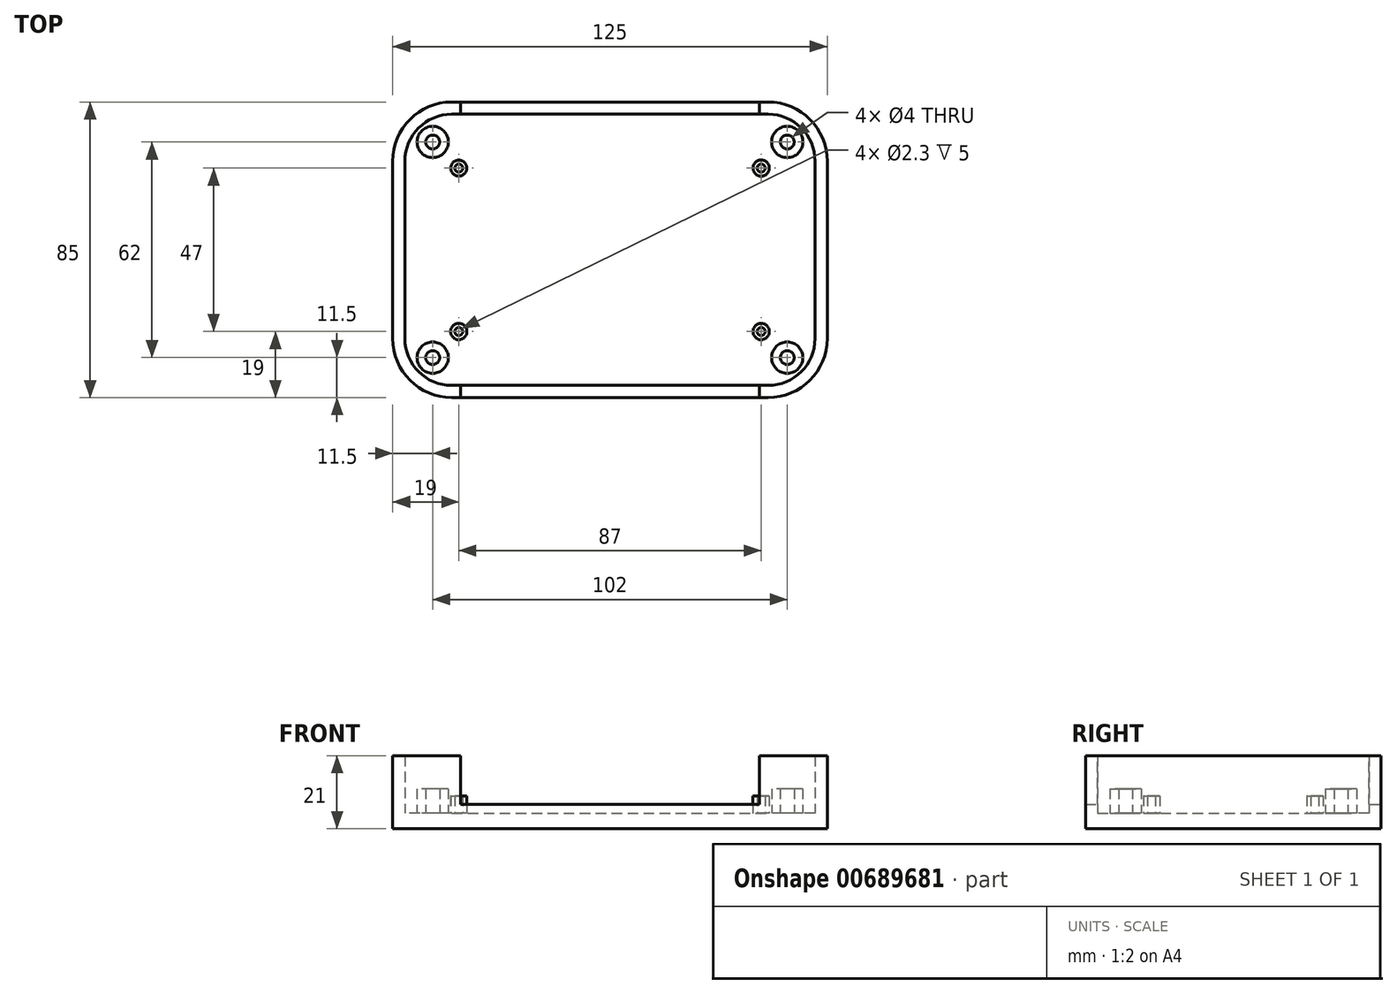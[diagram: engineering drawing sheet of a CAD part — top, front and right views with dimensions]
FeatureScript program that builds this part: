
annotation { "Feature Type Name" : "Feature", "Feature Type Description" : "" }
export const myFeature = defineFeature(function(context is Context, id is Id, definition is map)
    precondition{}
    {
        {
            var Q0;
            Q0=qCreatedBy(makeId("Top.planeOp"),FACE);
            var sketch = newSketch(context, id + "F0", { "sketchPlane" : qUnion([Q0])});
            skLineSegment(sketch, "E0.bottom", {"start": v(17, 0) * mm, "end": v(108, 0) * mm});
            skLineSegment(sketch, "E0.top", {"start": v(17, 85) * mm, "end": v(108, 85) * mm});
            skLineSegment(sketch, "E0.left", {"start": v(0, 17) * mm, "end": v(0, 68) * mm});
            skLineSegment(sketch, "E0.right", {"start": v(125, 17) * mm, "end": v(125, 68) * mm});
            skPoint(sketch, "E1.visualSharp", {"position": v(0, 85) * mm});
            skArc(sketch, "E1.filletArc", {"start": v(17, 85) * mm, "mid": v(4.98, 80.02) * mm, "end": v(0, 68) * mm});
            skPoint(sketch, "E2.visualSharp", {"position": v(125, 85) * mm});
            skArc(sketch, "E2.filletArc", {"start": v(125, 68) * mm, "mid": v(120.02, 80.02) * mm, "end": v(108, 85) * mm});
            skPoint(sketch, "E3.visualSharp", {"position": v(125, 0) * mm});
            skArc(sketch, "E3.filletArc", {"start": v(108, 0) * mm, "mid": v(120.02, 4.98) * mm, "end": v(125, 17) * mm});
            skPoint(sketch, "E4.visualSharp", {"position": v(0, 0) * mm});
            skArc(sketch, "E4.filletArc", {"start": v(0, 17) * mm, "mid": v(4.98, 4.98) * mm, "end": v(17, 0) * mm});
            skSolve(sketch);
        }
        {
            var Q0;
            Q0 = qSketchRegion(id + "F0", true);
            extrude(context, id + "F1", {"entities" : qUnion([Q0]), "oppositeDirection" : true, "depth" : 4.5 * mm, "offsetDistance" : 25.4 * mm});
        }
        {
            var Q0;
            Q0=qCreatedBy(makeId("Top.planeOp"),FACE);
            var sketch = newSketch(context, id + "F2", { "sketchPlane" : qUnion([Q0])});
            skCircle(sketch, "E5", {"center": v(11.5, 73.5) * mm, "radius": 4.5 * mm});
            skCircle(sketch, "E6", {"center": v(113.5, 73.5) * mm, "radius": 4.5 * mm});
            skCircle(sketch, "E7", {"center": v(11.5, 11.5) * mm, "radius": 4.5 * mm});
            skCircle(sketch, "E8", {"center": v(113.5, 11.5) * mm, "radius": 4.5 * mm});
            skCircle(sketch, "E9.0", {"center": v(11.5, 73.5) * mm, "radius": 2 * mm});
            skCircle(sketch, "E10", {"center": v(113.5, 73.5) * mm, "radius": 2 * mm});
            skCircle(sketch, "E11", {"center": v(11.5, 11.5) * mm, "radius": 2 * mm});
            skCircle(sketch, "E12", {"center": v(113.5, 11.5) * mm, "radius": 2 * mm});
            skSolve(sketch);
        }
        {
            var Q0;
            Q0 = qSketchRegion(id + "F2", true);
            extrude(context, id + "F3", {"entities" : qUnion([Q0]), "depth" : 7 * mm, "offsetDistance" : 25.4 * mm});
        }
        {
            var Q0;
            Q0=qCreatedBy(makeId("Top.planeOp"),FACE);
            var sketch = newSketch(context, id + "F4", { "sketchPlane" : qUnion([Q0])});
            skLineSegment(sketch, "E13.bottom", {"start": v(17, 0) * mm, "end": v(108, 0) * mm});
            skLineSegment(sketch, "E13.top", {"start": v(17, 85) * mm, "end": v(108, 85) * mm});
            skLineSegment(sketch, "E13.left", {"start": v(0, 17) * mm, "end": v(0, 68) * mm});
            skLineSegment(sketch, "E13.right", {"start": v(125, 17) * mm, "end": v(125, 68) * mm});
            skPoint(sketch, "E14.visualSharp", {"position": v(0, 85) * mm});
            skArc(sketch, "E14.filletArc", {"start": v(17, 85) * mm, "mid": v(4.98, 80.02) * mm, "end": v(0, 68) * mm});
            skPoint(sketch, "E15.visualSharp", {"position": v(0, 0) * mm});
            skArc(sketch, "E15.filletArc", {"start": v(0, 17) * mm, "mid": v(4.98, 4.98) * mm, "end": v(17, 0) * mm});
            skPoint(sketch, "E16.visualSharp", {"position": v(125, 0) * mm});
            skArc(sketch, "E16.filletArc", {"start": v(108, 0) * mm, "mid": v(120.02, 4.98) * mm, "end": v(125, 17) * mm});
            skPoint(sketch, "E17.visualSharp", {"position": v(125, 85) * mm});
            skArc(sketch, "E17.filletArc", {"start": v(125, 68) * mm, "mid": v(120.02, 80.02) * mm, "end": v(108, 85) * mm});
            skLineSegment(sketch, "E18.0", {"start": v(17, 81.5) * mm, "end": v(108, 81.5) * mm});
            skArc(sketch, "E18.1", {"start": v(121.5, 68) * mm, "mid": v(117.55, 77.55) * mm, "end": v(108, 81.5) * mm});
            skArc(sketch, "E18.2", {"start": v(17, 81.5) * mm, "mid": v(7.45, 77.55) * mm, "end": v(3.5, 68) * mm});
            skLineSegment(sketch, "E18.3", {"start": v(121.5, 17) * mm, "end": v(121.5, 68) * mm});
            skLineSegment(sketch, "E18.4", {"start": v(3.5, 17) * mm, "end": v(3.5, 68) * mm});
            skArc(sketch, "E18.5", {"start": v(3.5, 17) * mm, "mid": v(7.45, 7.45) * mm, "end": v(17, 3.5) * mm});
            skLineSegment(sketch, "E18.6", {"start": v(17, 3.5) * mm, "end": v(108, 3.5) * mm});
            skArc(sketch, "E18.7", {"start": v(108, 3.5) * mm, "mid": v(117.55, 7.45) * mm, "end": v(121.5, 17) * mm});
            skSolve(sketch);
        }
        {
            var Q0;
            Q0 = qSketchRegion(id + "F4", true);
            extrude(context, id + "F5", {"entities" : qUnion([Q0]), "operationType" : NewBodyOperationType.ADD, "depth" : 16.5 * mm, "offsetDistance" : 25.4 * mm});
        }
        {
            var Q0;
            Q0=qCreatedBy(makeId("Top.planeOp"),FACE);
            var sketch = newSketch(context, id + "F6", { "sketchPlane" : qUnion([Q0])});
            skCircle(sketch, "E19", {"center": v(19, 66) * mm, "radius": 2.3 * mm});
            skCircle(sketch, "E20", {"center": v(106, 66) * mm, "radius": 2.35 * mm});
            skCircle(sketch, "E21", {"center": v(106, 19) * mm, "radius": 2.35 * mm});
            skCircle(sketch, "E22", {"center": v(19, 19) * mm, "radius": 2.35 * mm});
            skCircle(sketch, "E23", {"center": v(19, 66) * mm, "radius": 1.15 * mm});
            skCircle(sketch, "E24", {"center": v(106, 66) * mm, "radius": 1.15 * mm});
            skCircle(sketch, "E25", {"center": v(106, 19) * mm, "radius": 1.15 * mm});
            skCircle(sketch, "E26", {"center": v(19, 19) * mm, "radius": 1.15 * mm});
            skSolve(sketch);
        }
        {
            var Q0;
            Q0 = qSketchRegion(id + "F6", true);
            extrude(context, id + "F7", {"entities" : qUnion([Q0]), "operationType" : NewBodyOperationType.ADD, "depth" : 5 * mm, "offsetDistance" : 25.4 * mm});
        }
        {
            var Q0;
            Q0=qCreatedBy(makeId("Top.planeOp"),FACE);
            cPlane(context, id + "F8", {"entities" : qUnion([Q0]), "cplaneType" : CPlaneType.OFFSET, "offset" : 2.5 * mm, "width" : 152.4 * mm, "height" : 152.4 * mm});
        }
        {
            var Q0;
            Q0=qCreatedBy(id+"F8.planeOp",FACE);
            var sketch = newSketch(context, id + "F9", { "sketchPlane" : qUnion([Q0])});
            skLineSegment(sketch, "E27.top", {"start": v(19.5, 85) * mm, "end": v(105.5, 85) * mm});
            skLineSegment(sketch, "E28.0", {"start": v(19.5, 0) * mm, "end": v(19.5, 11.67) * mm});
            skLineSegment(sketch, "E29.0", {"start": v(105.5, 0) * mm, "end": v(105.5, 11.67) * mm});
            skLineSegment(sketch, "E30.trimOffspring", {"start": v(19.5, 0) * mm, "end": v(105.5, 0) * mm});
            skLineSegment(sketch, "E31", {"start": v(19.5, 70.92) * mm, "end": v(105.5, 70.92) * mm});
            skLineSegment(sketch, "E32", {"start": v(19.5, 11.67) * mm, "end": v(105.5, 11.67) * mm});
            skLineSegment(sketch, "E33.trimOffspring", {"start": v(19.5, 70.92) * mm, "end": v(19.5, 85) * mm});
            skLineSegment(sketch, "E34.trimOffspring", {"start": v(105.5, 70.92) * mm, "end": v(105.5, 85) * mm});
            skSolve(sketch);
        }
        {
            var Q0;
            Q0 = qSketchRegion(id + "F9", true);
            extrude(context, id + "F10", {"entities" : qUnion([Q0]), "operationType" : NewBodyOperationType.REMOVE, "depth" : 50.8 * mm, "offsetDistance" : 25.4 * mm});
        }
    });
